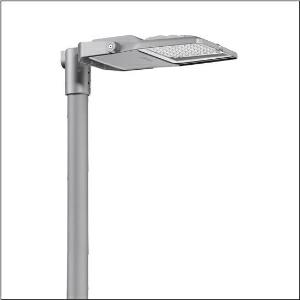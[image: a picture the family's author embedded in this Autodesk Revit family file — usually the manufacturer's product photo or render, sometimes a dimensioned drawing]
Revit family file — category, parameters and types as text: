
# Revit family: floodlight_fl_21_mini___pl43_5xa7775c2a3a_cdc0
name_source: partatom
category: Lighting Fixtures
units: mm (PartAtom-declared; Revit-internal decimal feet)

## family parameters
Cut with Voids When Loaded = No
Host = Face
Light Source = No
Part Type = Normal
Room Calculation Point = No
Round Connector Dimension = Use Diameter
Shared = No

## types (1)
- --- (1 x LED, 12500 lm, 89 W, 3000K)
    Apparent Load = 89 VA
    CIE Flux Codes = 27 78 99 100 100
    Color Rendering = 70
    Color Temperature = 3000K
    Default Elevation = 1800 mm
    Description = Floodlight FL 21 mini, floodlight, primary light control with lens, of PMMA, primary optical cover: protective disc, of toughened safety glass, transparent, light distribution: PL43, light emission: direct distribution, installation type: surface-mounted, LED, High Power LED, rated luminous flux: 12.500lm, luminous efficacy: 140lm/W, light colour: 730, colour temperature: 3000K, control: flexible luminous flux parameterisation, time-dependent luminous flux control, constant luminous flux control, overheat protection, presetting dimming logarithmic, with terminal, 6-pole, mains connection: 220..240V, AC, 50/60Hz, start of lifetime: 89W, end of service life: 94W, reduction: 43W, luminaire housing, of diecast aluminium, powder-coated, Siteco® metallic grey (DB 702S), corrosivity category C5 mid according to DIN EN ISO 12944, sealing non-destructively replaceable, please order mast flange separately, mast bracket, of steel, galvanised, powder-coated, Siteco® metallic grey (DB 702S), Smart Interface above, protection rating (complete): IP66, insulation class (complete): insulation class II (safety insulation), certification: CE, ENEC, VDE, protection symbol: D, impact resistance: IK08, permissible operating ambient temperature: -40..+40°C, permissible operating ambient temperature for outdoor applications: -40..+50°C, standard: DIN EN 12944, LABS conformity tested according to VDMA 24364:2018-05, packaging unit: 1 piece

Light Distribution: PL43
    Height = 70 mm
    Lamp = 1 x LED
    Lamp Light Flux = 12500 lm
    Lamp Power = 89 W
    Lamp count = 1
    Length = 485 mm
    Luminous efficacy = 140 lm/W
    Manufacturer = Siteco
    ModVariant = No
    Model = 5XA7775C2A3A
    Number of Poles = 1
    OnlyDefault = Yes
    Power Factor = 1
    Product Name = Floodlight FL 21 mini | PL43
    Product group = floodlight | pylon annexe
    ProductGroupID = 6200
    Protection Class = Protection class II
    Protection Degree = IP 66
    RLX_Detail_Level = 1
    RLX_Emergency_Light_Flux = 0 lm
    RLX_Emergency_Type = 0
    RLX_Emergency_Type_DB = No
    RlxData = <blob elided: 100741 chars, md5=0405c88b>
    Socket = socket
    Standby Power = 0 W
    System Light Flux = 12500 lm
    System Power = 89 W
    Type Comments = factory setting: luminous flux: 100 % | dim-lin: 254 | 456 mA
    Type Image = l_1007125.jpg
    URL = http://relux.com
    VarID = @adj_111279
    Voltage = 0 V
    Weight = 0.00 kg
    Width = 337 mm

## geometry (parser evidence)
native form markers: Blend x4, Sweep x12
no freeform markers — native parametric forms only
